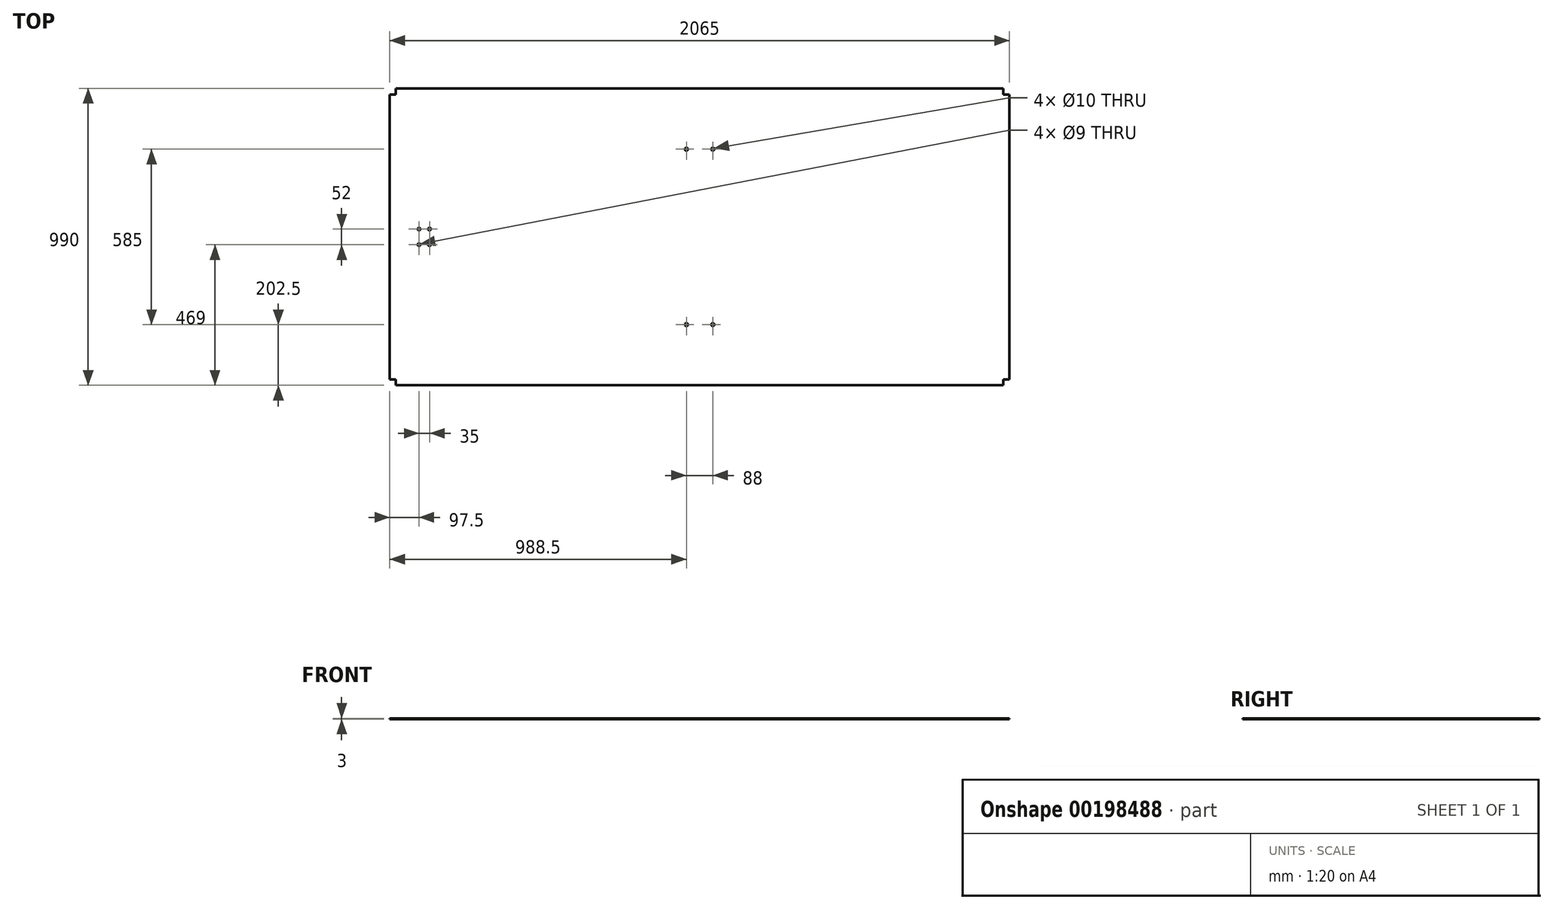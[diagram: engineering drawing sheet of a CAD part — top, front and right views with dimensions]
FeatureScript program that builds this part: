
annotation { "Feature Type Name" : "Feature", "Feature Type Description" : "" }
export const myFeature = defineFeature(function(context is Context, id is Id, definition is map)
    precondition{}
    {
        {
            var Q0;
            Q0=qCreatedBy(makeId("Top.planeOp"),FACE);
            var sketch = newSketch(context, id + "F0", { "sketchPlane" : qUnion([Q0])});
            skLineSegment(sketch, "E0.bottom", {"start": v(1032.5, -475) * mm, "end": v(-1032.5, -475) * mm});
            skLineSegment(sketch, "E0.top", {"start": v(1032.5, 475) * mm, "end": v(-1032.5, 475) * mm});
            skLineSegment(sketch, "E0.left", {"start": v(1032.5, -475) * mm, "end": v(1032.5, 475) * mm});
            skLineSegment(sketch, "E0.right", {"start": v(-1032.5, -475) * mm, "end": v(-1032.5, 475) * mm});
            skPoint(sketch, "E0.middle", {"position": v(0, 0) * mm});
            skSolve(sketch);
        }
        {
            var Q0;
            Q0 = qSketchRegion(id + "F0", true);
            extrude(context, id + "F1", {"entities" : qUnion([Q0]), "depth" : 3 * mm});
        }
        {
            var Q0;
            Q0=makeQuery(id+"F1.opExtrude","CAP_FACE",FACE,{"disambiguationData":[OSD([sQuery(id+"F0.wireOp",EDGE,"E0.bottom"),sQuery(id+"F0.wireOp",EDGE,"E0.top"),sQuery(id+"F0.wireOp",EDGE,"E0.left"),sQuery(id+"F0.wireOp",EDGE,"E0.right")])],"isStart":false});
            var sketch = newSketch(context, id + "F2", { "sketchPlane" : qUnion([Q0])});
            skCircle(sketch, "E1", {"center": v(-44, -292.5) * mm, "radius": 5 * mm});
            skCircle(sketch, "E2", {"center": v(44, -292.5) * mm, "radius": 5 * mm});
            skSolve(sketch);
        }
        {
            var Q0;
            Q0 = qSketchRegion(id + "F2", true);
            extrude(context, id + "F3", {"entities" : qUnion([Q0]), "operationType" : NewBodyOperationType.REMOVE, "endBound" : BoundingType.UP_TO_NEXT, "oppositeDirection" : true, "depth" : 25 * mm});
        }
        {
            var Q0;
            Q0=makeQuery(id+"F3.boolean.opBoolean","COPY",FACE,{"derivedFrom":makeQuery(id+"F3.opExtrude","SWEPT_FACE",FACE,{"disambiguationData":[OSD([sQuery(id+"F2.wireOp",EDGE,"E1")])]})});
            var Q1;
            Q1=makeQuery(id+"F3.boolean.opBoolean","COPY",FACE,{"derivedFrom":makeQuery(id+"F3.opExtrude","SWEPT_FACE",FACE,{"disambiguationData":[OSD([sQuery(id+"F2.wireOp",EDGE,"E2")])]})});
            var Q2;
            Q2=qCreatedBy(makeId("Front.planeOp"),FACE);
            mirror(context, id + "F4", {"patternType" : MirrorType.FACE, "faces" : qUnion([Q0, Q1]), "mirrorPlane" : qUnion([Q2])});
        }
        {
            var Q0;
            Q0=makeQuery(id+"F1.opExtrude","CAP_FACE",FACE,{"disambiguationData":[OSD([sQuery(id+"F0.wireOp",EDGE,"E0.bottom"),sQuery(id+"F0.wireOp",EDGE,"E0.top"),sQuery(id+"F0.wireOp",EDGE,"E0.left"),sQuery(id+"F0.wireOp",EDGE,"E0.right")])],"isStart":false});
            var sketch = newSketch(context, id + "F5", { "sketchPlane" : qUnion([Q0])});
            skCircle(sketch, "E3", {"center": v(-935, -26) * mm, "radius": 4.5 * mm});
            skCircle(sketch, "E4", {"center": v(-935, 26) * mm, "radius": 4.5 * mm});
            skCircle(sketch, "E5", {"center": v(-900, -26) * mm, "radius": 4.5 * mm});
            skCircle(sketch, "E6", {"center": v(-900, 26) * mm, "radius": 4.5 * mm});
            skLineSegment(sketch, "E7", {"start": v(-935, 26) * mm, "end": v(-900, 26) * mm, "construction": true});
            skLineSegment(sketch, "E8", {"start": v(-900, -26) * mm, "end": v(-900, 26) * mm, "construction": true});
            skLineSegment(sketch, "E9", {"start": v(-935, -26) * mm, "end": v(-935, 26) * mm, "construction": true});
            skLineSegment(sketch, "E10", {"start": v(-935, -26) * mm, "end": v(-900, -26) * mm, "construction": true});
            skLineSegment(sketch, "E11", {"start": v(-900, 0) * mm, "end": v(0, 0) * mm, "construction": true});
            skSolve(sketch);
        }
        {
            var Q0;
            Q0 = qSketchRegion(id + "F5", true);
            extrude(context, id + "F6", {"entities" : qUnion([Q0]), "operationType" : NewBodyOperationType.REMOVE, "endBound" : BoundingType.UP_TO_NEXT, "oppositeDirection" : true, "depth" : 25 * mm});
        }
        {
            var Q0;
            Q0=makeQuery(id+"F1.opExtrude","SWEPT_FACE",FACE,{"disambiguationData":[OSD([sQuery(id+"F0.wireOp",EDGE,"E0.bottom")])]});
            var sketch = newSketch(context, id + "F7", { "sketchPlane" : qUnion([Q0])});
            skLineSegment(sketch, "E12.bottom", {"start": v(-1012.5, 3) * mm, "end": v(1012.5, 3) * mm});
            skLineSegment(sketch, "E12.top", {"start": v(-1012.5, 0) * mm, "end": v(1012.5, 0) * mm});
            skLineSegment(sketch, "E12.left", {"start": v(-1012.5, 3) * mm, "end": v(-1012.5, 0) * mm});
            skLineSegment(sketch, "E12.right", {"start": v(1012.5, 3) * mm, "end": v(1012.5, 0) * mm});
            skSolve(sketch);
        }
        {
            var Q0;
            Q0 = qSketchRegion(id + "F7", true);
            extrude(context, id + "F8", {"entities" : qUnion([Q0]), "operationType" : NewBodyOperationType.ADD, "depth" : 20 * mm});
        }
        {
            var Q0;
            Q0=makeQuery(id+"F1.opExtrude","SWEPT_FACE",FACE,{"disambiguationData":[OSD([sQuery(id+"F0.wireOp",EDGE,"E0.top")])]});
            var sketch = newSketch(context, id + "F9", { "sketchPlane" : qUnion([Q0])});
            skLineSegment(sketch, "E13.bottom", {"start": v(-1012.5, 3) * mm, "end": v(1012.5, 3) * mm});
            skLineSegment(sketch, "E13.top", {"start": v(-1012.5, 0) * mm, "end": v(1012.5, 0) * mm});
            skLineSegment(sketch, "E13.left", {"start": v(-1012.5, 3) * mm, "end": v(-1012.5, 0) * mm});
            skLineSegment(sketch, "E13.right", {"start": v(1012.5, 3) * mm, "end": v(1012.5, 0) * mm});
            skSolve(sketch);
        }
        {
            var Q0;
            Q0 = qSketchRegion(id + "F9", true);
            extrude(context, id + "F10", {"entities" : qUnion([Q0]), "operationType" : NewBodyOperationType.ADD, "depth" : 20 * mm});
        }
    });
